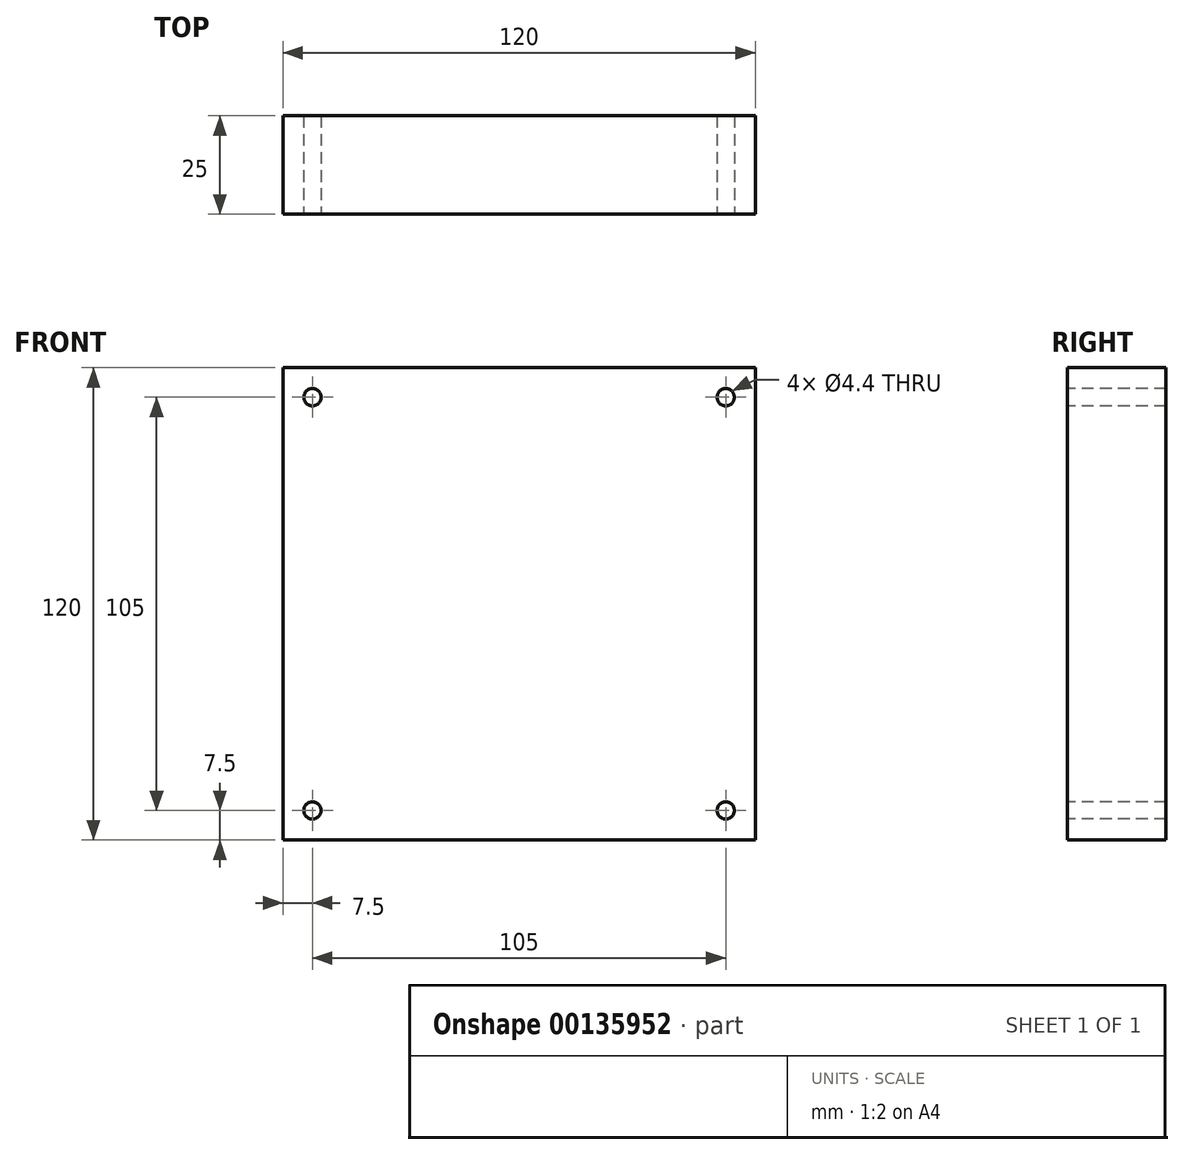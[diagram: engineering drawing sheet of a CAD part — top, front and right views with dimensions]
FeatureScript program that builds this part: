
annotation { "Feature Type Name" : "Feature", "Feature Type Description" : "" }
export const myFeature = defineFeature(function(context is Context, id is Id, definition is map)
    precondition{}
    {
        {
            var Q0;
            Q0=qCreatedBy(makeId("Front.planeOp"),FACE);
            var sketch = newSketch(context, id + "F0", { "sketchPlane" : qUnion([Q0])});
            skLineSegment(sketch, "E0.bottom", {"start": v(60, -60) * mm, "end": v(-60, -60) * mm});
            skLineSegment(sketch, "E0.top", {"start": v(60, 60) * mm, "end": v(-60, 60) * mm});
            skLineSegment(sketch, "E0.left", {"start": v(60, -60) * mm, "end": v(60, 60) * mm});
            skLineSegment(sketch, "E0.right", {"start": v(-60, -60) * mm, "end": v(-60, 60) * mm});
            skPoint(sketch, "E0.middle", {"position": v(0, 0) * mm});
            skSolve(sketch);
        }
        {
            var Q0;
            Q0 = qSketchRegion(id + "F0", true);
            extrude(context, id + "F1", {"entities" : qUnion([Q0]), "endBound" : BoundingType.SYMMETRIC, "depth" : 25 * mm});
        }
        {
            var Q0;
            Q0=makeQuery(id+"F1.opExtrude","CAP_FACE",FACE,{"disambiguationData":[OSD([sQuery(id+"F0.wireOp",EDGE,"E0.bottom"),sQuery(id+"F0.wireOp",EDGE,"E0.top"),sQuery(id+"F0.wireOp",EDGE,"E0.left"),sQuery(id+"F0.wireOp",EDGE,"E0.right")])],"isStart":false});
            var sketch = newSketch(context, id + "F2", { "sketchPlane" : qUnion([Q0])});
            skCircle(sketch, "E1", {"center": v(-52.5, -52.5) * mm, "radius": 2 * mm});
            skCircle(sketch, "E2.MirrorC", {"center": v(52.5, -52.5) * mm, "radius": 2 * mm});
            skCircle(sketch, "E3.MirrorC", {"center": v(-52.5, 52.5) * mm, "radius": 2 * mm});
            skCircle(sketch, "E4.MirrorC", {"center": v(52.5, 52.5) * mm, "radius": 2 * mm});
            skSolve(sketch);
        }
        {
            var Q0;
            Q0=sQuery(id+"F2.wireOp",VERTEX,"E2.MirrorC.center");
            var Q1;
            Q1=sQuery(id+"F2.wireOp",VERTEX,"E1.center");
            var Q2;
            Q2=sQuery(id+"F2.wireOp",VERTEX,"E3.MirrorC.center");
            var Q3;
            Q3=sQuery(id+"F2.wireOp",VERTEX,"E4.MirrorC.center");
            var Q4;
            Q4=makeQuery(id+"F1.opExtrude","SWEPT_BODY",BODY,{"disambiguationData":[OSD([sQuery(id+"F0.wireOp",EDGE,"E0.bottom"),sQuery(id+"F0.wireOp",EDGE,"E0.top"),sQuery(id+"F0.wireOp",EDGE,"E0.left"),sQuery(id+"F0.wireOp",EDGE,"E0.right")])]});
            hole(context, id + "F3", {"style" : HoleStyle.SIMPLE, "endStyle" : HoleEndStyle.THROUGH, "standardTappedOrClearance" : lookupTablePath({ "standard" : "ISO", "fit" : "Normal", "size" : "M4", "type" : "Clearance" }), "standardBlindInLast" : lookupTablePath({ "fit" : "Standard", "standard" : "ISO", "size" : "M4", "type" : "Clearance" }), "holeDiameter" : 4.4 * mm, "startFromSketch" : true, "locations" : qUnion([Q0, Q1, Q2, Q3]), "scope" : qUnion([Q4]), "isTappedThrough" : true});
        }
    });
